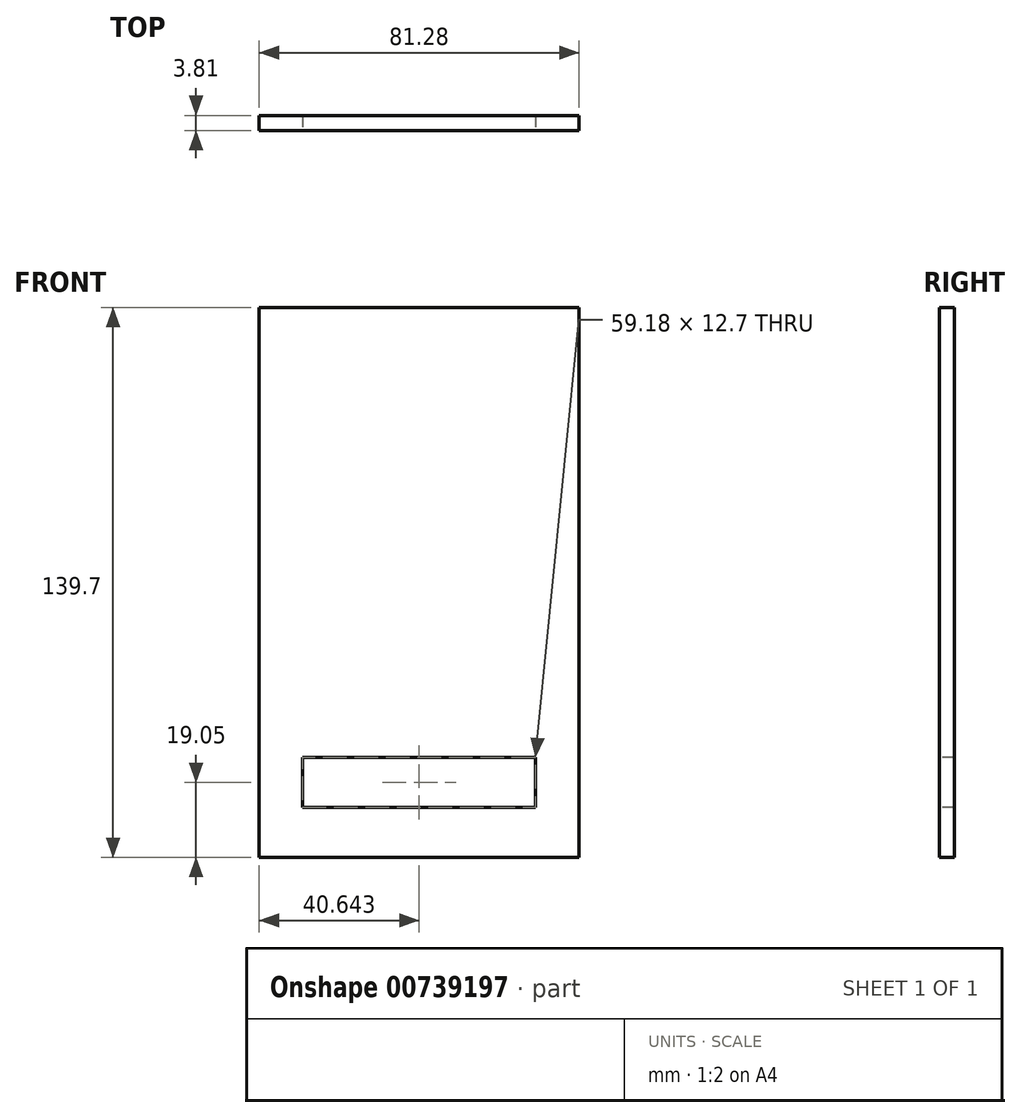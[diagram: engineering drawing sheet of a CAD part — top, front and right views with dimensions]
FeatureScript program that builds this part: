
annotation { "Feature Type Name" : "Feature", "Feature Type Description" : "" }
export const myFeature = defineFeature(function(context is Context, id is Id, definition is map)
    precondition{}
    {
        {
            var Q0;
            Q0=qCreatedBy(makeId("Front.planeOp"),FACE);
            var sketch = newSketch(context, id + "F0", { "sketchPlane" : qUnion([Q0])});
            skLineSegment(sketch, "E0", {"start": v(0, 0) * mm, "end": v(81.28, 0) * mm});
            skLineSegment(sketch, "E1", {"start": v(81.28, 0) * mm, "end": v(81.28, -139.7) * mm});
            skLineSegment(sketch, "E2", {"start": v(81.28, -139.7) * mm, "end": v(0, -139.7) * mm});
            skLineSegment(sketch, "E3", {"start": v(0, -139.7) * mm, "end": v(0, 0) * mm});
            skLineSegment(sketch, "E4", {"start": v(0, -139.7) * mm, "end": v(0, -127) * mm});
            skLineSegment(sketch, "E5", {"start": v(11.06, -127) * mm, "end": v(70.23, -127) * mm});
            skLineSegment(sketch, "E6", {"start": v(81.28, -127) * mm, "end": v(81.28, -114.3) * mm});
            skLineSegment(sketch, "E7", {"start": v(70.23, -114.3) * mm, "end": v(11.06, -114.3) * mm});
            skLineSegment(sketch, "E8", {"start": v(0, -114.3) * mm, "end": v(0, -127) * mm});
            skLineSegment(sketch, "E9", {"start": v(11.06, -114.3) * mm, "end": v(11.06, -127) * mm});
            skLineSegment(sketch, "E10", {"start": v(70.23, -114.3) * mm, "end": v(70.23, -127) * mm});
            skSolve(sketch);
        }
        {
            var Q0;
            {var subQ1=sQuery(id+"F0.wireOp",EDGE,"E0");Q0=makeQuery(id+"F0.imprint","IMPRINT",FACE,{"disambiguationData":[TD([[makeQuery(id+"F0.imprint","IMPRINT",EDGE,{"derivedFrom":subQ1}),-1.0]])]});}
            extrude(context, id + "F1", {"entities" : qUnion([Q0]), "oppositeDirection" : true, "depth" : 3.8 * mm, "offsetDistance" : 25.4 * mm});
        }
    });
